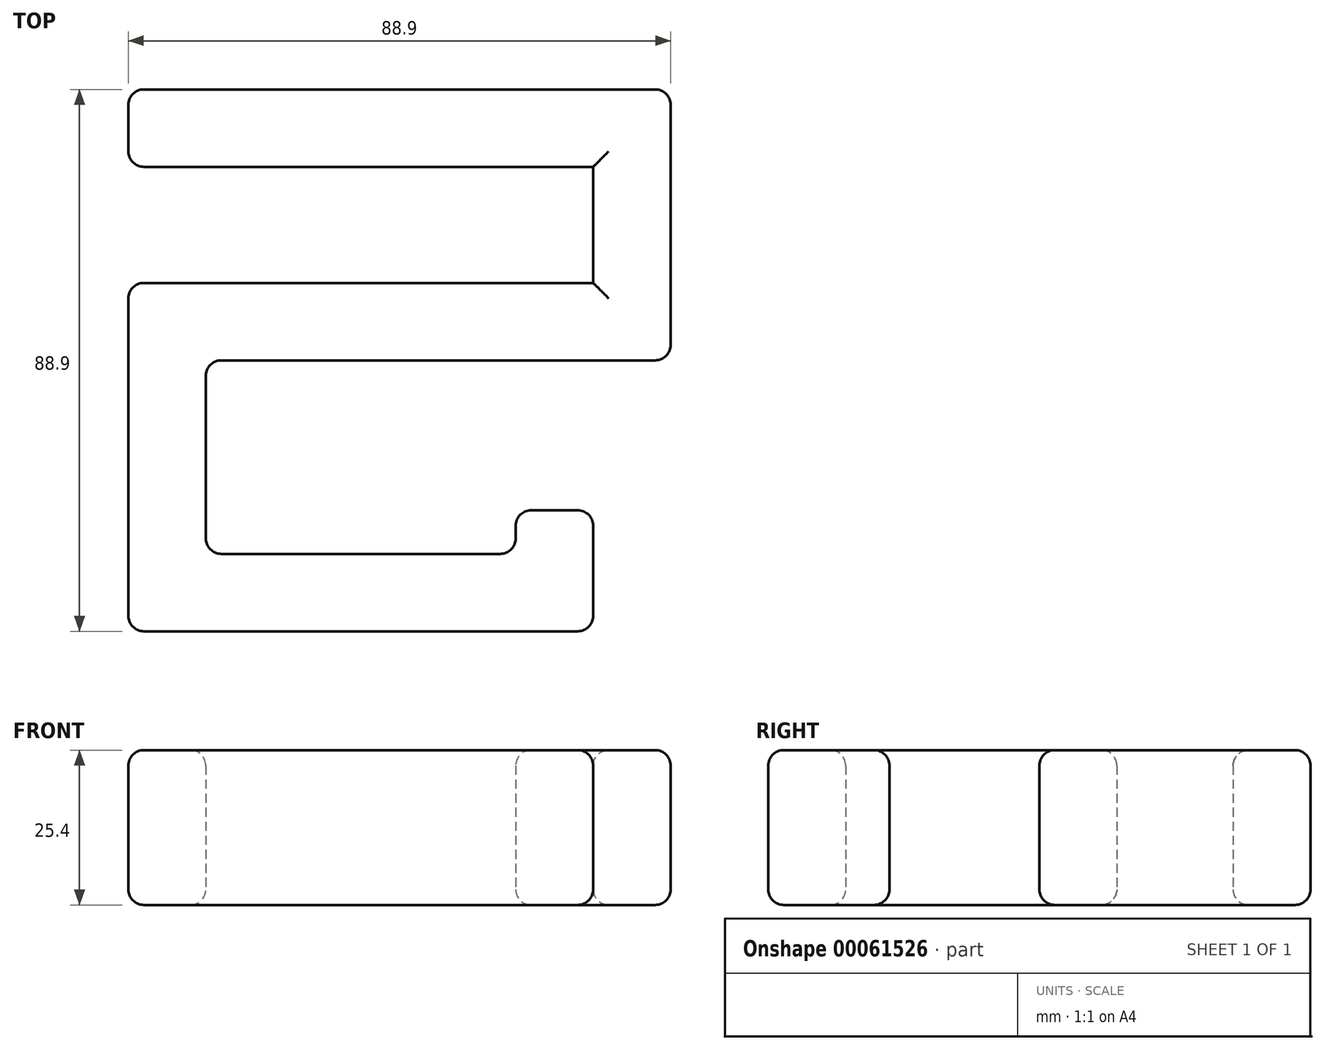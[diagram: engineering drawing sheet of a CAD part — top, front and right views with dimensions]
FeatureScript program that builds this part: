
annotation { "Feature Type Name" : "Feature", "Feature Type Description" : "" }
export const myFeature = defineFeature(function(context is Context, id is Id, definition is map)
    precondition{}
    {
        {
            var Q0;
            Q0=qCreatedBy(makeId("Top.planeOp"),FACE);
            var sketch = newSketch(context, id + "F0", { "sketchPlane" : qUnion([Q0])});
            skLineSegment(sketch, "E0", {"start": v(-38.44, 51.6) * mm, "end": v(50.46, 51.6) * mm});
            skLineSegment(sketch, "E1", {"start": v(50.46, 51.6) * mm, "end": v(50.46, 7.15) * mm});
            skLineSegment(sketch, "E2", {"start": v(50.46, 7.15) * mm, "end": v(-25.74, 7.15) * mm});
            skLineSegment(sketch, "E3", {"start": v(-25.74, 7.15) * mm, "end": v(-25.74, -24.6) * mm});
            skLineSegment(sketch, "E4", {"start": v(-25.74, -24.6) * mm, "end": v(25.06, -24.6) * mm});
            skLineSegment(sketch, "E5", {"start": v(25.06, -24.6) * mm, "end": v(25.06, -17.44) * mm});
            skLineSegment(sketch, "E6", {"start": v(25.06, -17.44) * mm, "end": v(37.76, -17.44) * mm});
            skLineSegment(sketch, "E7", {"start": v(37.76, -17.44) * mm, "end": v(37.76, -37.3) * mm});
            skLineSegment(sketch, "E8", {"start": v(37.76, -37.3) * mm, "end": v(-38.44, -37.3) * mm});
            skLineSegment(sketch, "E9", {"start": v(-38.44, -37.3) * mm, "end": v(-38.44, 19.85) * mm});
            skLineSegment(sketch, "E10", {"start": v(-38.44, 19.85) * mm, "end": v(37.76, 19.85) * mm});
            skLineSegment(sketch, "E11", {"start": v(37.76, 19.85) * mm, "end": v(37.76, 38.9) * mm});
            skLineSegment(sketch, "E12", {"start": v(37.76, 38.9) * mm, "end": v(-38.44, 38.9) * mm});
            skLineSegment(sketch, "E13", {"start": v(-38.44, 38.9) * mm, "end": v(-38.44, 51.6) * mm});
            skSolve(sketch);
        }
        {
            var Q0;
            Q0=makeQuery(id+"F0.imprint","IMPRINT",FACE,{"disambiguationData":[TD([[makeQuery(id+"F0.imprint","IMPRINT",EDGE,{"derivedFrom":sQuery(id+"F0.wireOp",EDGE,"E0")}),-1.0]])]});
            extrude(context, id + "F1", {"entities" : qUnion([Q0]), "depth" : 25.4 * mm});
        }
        {
            var Q0;
            Q0=makeQuery(id+"F1.opExtrude","SWEPT_EDGE",EDGE,{"disambiguationData":[OSD([sQuery(id+"F0.wireOp",EDGE,"E0"),sQuery(id+"F0.wireOp",EDGE,"E13")])]});
            var Q1;
            Q1=makeQuery(id+"F1.opExtrude","SWEPT_EDGE",EDGE,{"disambiguationData":[OSD([sQuery(id+"F0.wireOp",EDGE,"E0"),sQuery(id+"F0.wireOp",EDGE,"E1")])]});
            var Q2;
            Q2=makeQuery(id+"F1.opExtrude","SWEPT_EDGE",EDGE,{"disambiguationData":[OSD([sQuery(id+"F0.wireOp",EDGE,"E1"),sQuery(id+"F0.wireOp",EDGE,"E2")])]});
            var Q3;
            Q3=makeQuery(id+"F1.opExtrude","SWEPT_EDGE",EDGE,{"disambiguationData":[OSD([sQuery(id+"F0.wireOp",EDGE,"E9"),sQuery(id+"F0.wireOp",EDGE,"E10")])]});
            var Q4;
            Q4=makeQuery(id+"F1.opExtrude","SWEPT_EDGE",EDGE,{"disambiguationData":[OSD([sQuery(id+"F0.wireOp",EDGE,"E8"),sQuery(id+"F0.wireOp",EDGE,"E9")])]});
            var Q5;
            Q5=makeQuery(id+"F1.opExtrude","SWEPT_EDGE",EDGE,{"disambiguationData":[OSD([sQuery(id+"F0.wireOp",EDGE,"E7"),sQuery(id+"F0.wireOp",EDGE,"E8")])]});
            var Q6;
            Q6=makeQuery(id+"F1.opExtrude","SWEPT_EDGE",EDGE,{"disambiguationData":[OSD([sQuery(id+"F0.wireOp",EDGE,"E5"),sQuery(id+"F0.wireOp",EDGE,"E6")])]});
            var Q7;
            Q7=makeQuery(id+"F1.opExtrude","SWEPT_EDGE",EDGE,{"disambiguationData":[OSD([sQuery(id+"F0.wireOp",EDGE,"E6"),sQuery(id+"F0.wireOp",EDGE,"E7")])]});
            var Q8;
            Q8=makeQuery(id+"F1.opExtrude","SWEPT_EDGE",EDGE,{"disambiguationData":[OSD([sQuery(id+"F0.wireOp",EDGE,"E2"),sQuery(id+"F0.wireOp",EDGE,"E3")])]});
            var Q9;
            Q9=makeQuery(id+"F1.opExtrude","SWEPT_EDGE",EDGE,{"disambiguationData":[OSD([sQuery(id+"F0.wireOp",EDGE,"E3"),sQuery(id+"F0.wireOp",EDGE,"E4")])]});
            var Q10;
            Q10=makeQuery(id+"F1.opExtrude","SWEPT_EDGE",EDGE,{"disambiguationData":[OSD([sQuery(id+"F0.wireOp",EDGE,"E4"),sQuery(id+"F0.wireOp",EDGE,"E5")])]});
            var Q11;
            Q11=makeQuery(id+"F1.opExtrude","SWEPT_EDGE",EDGE,{"disambiguationData":[OSD([sQuery(id+"F0.wireOp",EDGE,"E12"),sQuery(id+"F0.wireOp",EDGE,"E13")])]});
            var Q12;
            Q12=makeQuery(id+"F1.opExtrude","CAP_FACE",FACE,{"disambiguationData":[OSD([sQuery(id+"F0.wireOp",EDGE,"E0"),sQuery(id+"F0.wireOp",EDGE,"E1"),sQuery(id+"F0.wireOp",EDGE,"E2"),sQuery(id+"F0.wireOp",EDGE,"E3"),sQuery(id+"F0.wireOp",EDGE,"E4"),sQuery(id+"F0.wireOp",EDGE,"E5"),sQuery(id+"F0.wireOp",EDGE,"E6"),sQuery(id+"F0.wireOp",EDGE,"E7"),sQuery(id+"F0.wireOp",EDGE,"E8"),sQuery(id+"F0.wireOp",EDGE,"E9"),sQuery(id+"F0.wireOp",EDGE,"E10"),sQuery(id+"F0.wireOp",EDGE,"E11"),sQuery(id+"F0.wireOp",EDGE,"E12"),sQuery(id+"F0.wireOp",EDGE,"E13")])],"isStart":false});
            var Q13;
            Q13=makeQuery(id+"F1.opExtrude","CAP_FACE",FACE,{"disambiguationData":[OSD([sQuery(id+"F0.wireOp",EDGE,"E0"),sQuery(id+"F0.wireOp",EDGE,"E1"),sQuery(id+"F0.wireOp",EDGE,"E2"),sQuery(id+"F0.wireOp",EDGE,"E3"),sQuery(id+"F0.wireOp",EDGE,"E4"),sQuery(id+"F0.wireOp",EDGE,"E5"),sQuery(id+"F0.wireOp",EDGE,"E6"),sQuery(id+"F0.wireOp",EDGE,"E7"),sQuery(id+"F0.wireOp",EDGE,"E8"),sQuery(id+"F0.wireOp",EDGE,"E9"),sQuery(id+"F0.wireOp",EDGE,"E10"),sQuery(id+"F0.wireOp",EDGE,"E11"),sQuery(id+"F0.wireOp",EDGE,"E12"),sQuery(id+"F0.wireOp",EDGE,"E13")])],"isStart":true});
            fillet(context, id + "F2", {"entities" : qUnion([Q0, Q1, Q2, Q3, Q4, Q5, Q6, Q7, Q8, Q9, Q10, Q11, Q12, Q13]), "radius" : 2.54 * mm, "tangentPropagation" : true, "allowEdgeOverflow" : false});
        }
    });
